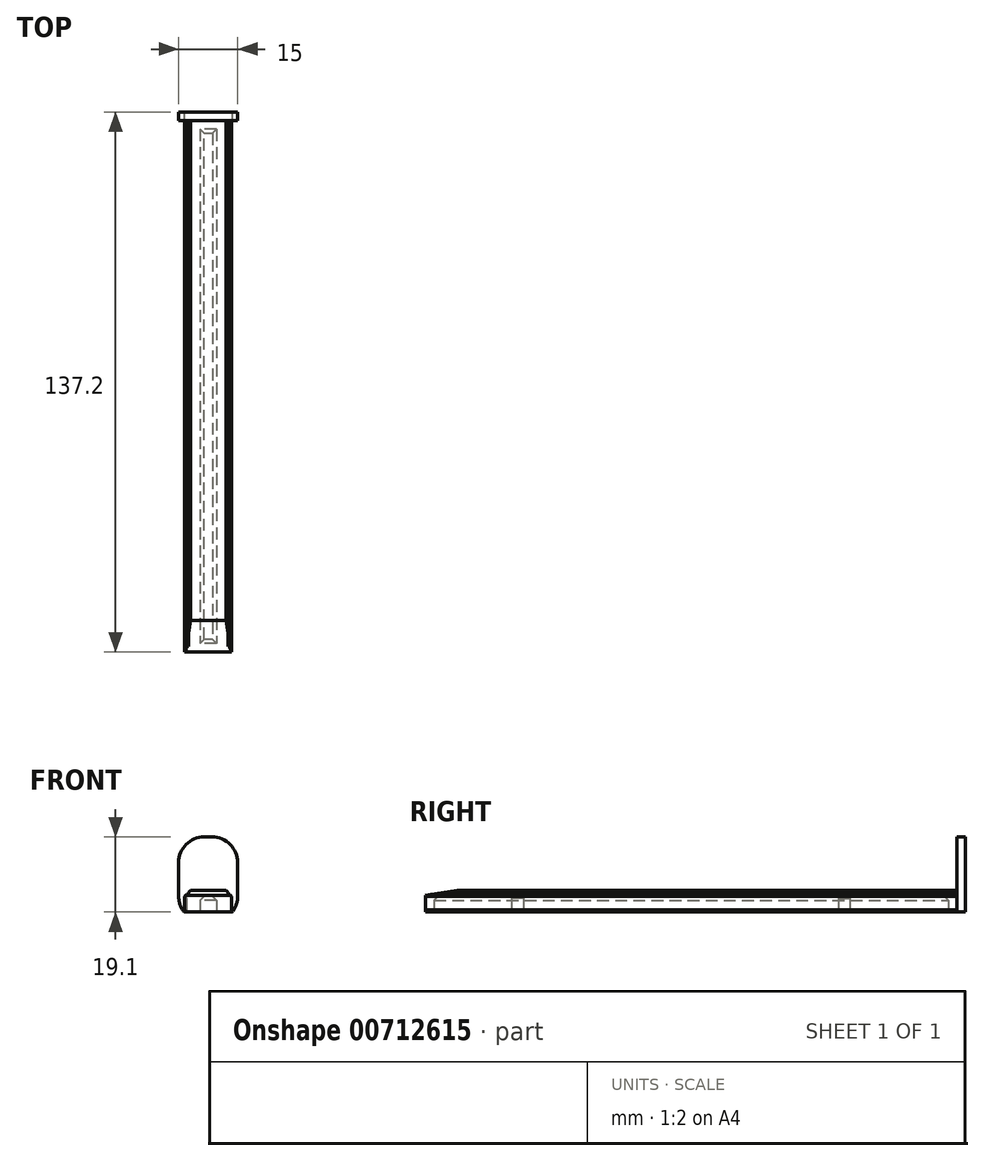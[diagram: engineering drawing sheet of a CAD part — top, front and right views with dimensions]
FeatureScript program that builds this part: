
annotation { "Feature Type Name" : "Feature", "Feature Type Description" : "" }
export const myFeature = defineFeature(function(context is Context, id is Id, definition is map)
    precondition{}
    {
        {
            var Q0;
            Q0=qCreatedBy(makeId("Front.planeOp"),FACE);
            var sketch = newSketch(context, id + "F0", { "sketchPlane" : qUnion([Q0])});
            skLineSegment(sketch, "E0.bottom", {"start": v(6, -2.75) * mm, "end": v(-6, -2.75) * mm});
            skLineSegment(sketch, "E0.top", {"start": v(5, 2.75) * mm, "end": v(-5, 2.75) * mm});
            skLineSegment(sketch, "E0.left", {"start": v(6, -2.75) * mm, "end": v(6, 1.75) * mm});
            skLineSegment(sketch, "E0.right", {"start": v(-6, -2.75) * mm, "end": v(-6, 1.75) * mm});
            skPoint(sketch, "E0.middle", {"position": v(0, 0) * mm});
            skLineSegment(sketch, "E1", {"start": v(-6, 1.75) * mm, "end": v(-5, 1.75) * mm});
            skLineSegment(sketch, "E2", {"start": v(-5, 2.75) * mm, "end": v(-5, 1.75) * mm});
            skLineSegment(sketch, "E3.MirrorCS", {"start": v(5, 2.75) * mm, "end": v(5, 1.75) * mm});
            skLineSegment(sketch, "E4.trimOffspring", {"start": v(5, 1.75) * mm, "end": v(6, 1.75) * mm});
            skPoint(sketch, "E5.orphan", {"position": v(-6, 2.75) * mm});
            skPoint(sketch, "E6.orphan", {"position": v(6, 2.75) * mm});
            skSolve(sketch);
        }
        {
            var Q0;
            Q0 = qSketchRegion(id + "F0", true);
            extrude(context, id + "F1", {"entities" : qUnion([Q0]), "depth" : 135 * mm, "offsetDistance" : 25 * mm});
        }
        {
            var Q0;
            Q0=makeQuery(id+"F1.opExtrude","CAP_EDGE",EDGE,{"disambiguationData":[OSD([sQuery(id+"F0.wireOp",EDGE,"E0.top")])],"isStart":false});
            chamfer(context, id + "F2", {"entities" : qUnion([Q0]), "chamferType" : ChamferType.TWO_OFFSETS, "width1" : 1.2 * mm, "oppositeDirection" : false, "width2" : 8 * mm, "tangentPropagation" : true});
        }
        {
            var Q0;
            Q0=qCreatedBy(makeId("Front.planeOp"),FACE);
            var sketch = newSketch(context, id + "F3", { "sketchPlane" : qUnion([Q0])});
            skLineSegment(sketch, "E7.bottom", {"start": v(1, -5.25) * mm, "end": v(-1, -5.25) * mm, "construction": true});
            skLineSegment(sketch, "E7.top", {"start": v(1, 16.35) * mm, "end": v(-1, 16.35) * mm});
            skLineSegment(sketch, "E7.left", {"start": v(7.5, 1.25) * mm, "end": v(7.5, 9.85) * mm});
            skLineSegment(sketch, "E7.right", {"start": v(-7.5, 1.25) * mm, "end": v(-7.5, 9.85) * mm});
            skLineSegment(sketch, "E8.0", {"start": v(6, -2.75) * mm, "end": v(-6, -2.75) * mm, "construction": true});
            skLineSegment(sketch, "E9.0", {"start": v(5, 2.75) * mm, "end": v(-5, 2.75) * mm, "construction": true});
            skPoint(sketch, "E10.visualSharp", {"position": v(7.5, 16.35) * mm});
            skArc(sketch, "E10.filletArc", {"start": v(7.5, 9.85) * mm, "mid": v(5.6, 14.45) * mm, "end": v(1, 16.35) * mm});
            skPoint(sketch, "E11.visualSharp", {"position": v(-7.5, 16.35) * mm});
            skArc(sketch, "E11.filletArc", {"start": v(-1, 16.35) * mm, "mid": v(-5.6, 14.45) * mm, "end": v(-7.5, 9.85) * mm});
            skPoint(sketch, "E12.visualSharp", {"position": v(-7.5, -5.25) * mm});
            skArc(sketch, "E12.filletArc", {"start": v(-7.5, 1.25) * mm, "mid": v(-7.15, -0.87) * mm, "end": v(-6.12, -2.75) * mm});
            skPoint(sketch, "E13.visualSharp", {"position": v(7.5, -5.25) * mm});
            skArc(sketch, "E13.filletArc", {"start": v(1, -5.25) * mm, "mid": v(3.85, -4.6) * mm, "end": v(6.12, -2.75) * mm, "construction": true});
            skLineSegment(sketch, "E14", {"start": v(-6.12, -2.75) * mm, "end": v(6.12, -2.75) * mm});
            skArc(sketch, "E15", {"start": v(6.12, -2.75) * mm, "mid": v(7.15, -0.87) * mm, "end": v(7.5, 1.25) * mm});
            skArc(sketch, "E16", {"start": v(-6.12, -2.75) * mm, "mid": v(-3.85, -4.6) * mm, "end": v(-1, -5.25) * mm, "construction": true});
            skSolve(sketch);
        }
        {
            var Q0;
            Q0 = qSketchRegion(id + "F3", true);
            extrude(context, id + "F4", {"entities" : qUnion([Q0]), "operationType" : NewBodyOperationType.ADD, "oppositeDirection" : true, "depth" : 2.2 * mm, "offsetDistance" : 25 * mm});
        }
        {
            var Q0;
            Q0=makeQuery(id+"F1.opExtrude","SWEPT_FACE",FACE,{"disambiguationData":[OSD([sQuery(id+"F0.wireOp",EDGE,"E0.right")])]});
            var sketch = newSketch(context, id + "F5", { "sketchPlane" : qUnion([Q0])});
            skLineSegment(sketch, "E17.0", {"start": v(0, -2.75) * mm, "end": v(0, -2.75) * mm});
            skLineSegment(sketch, "E18.0", {"start": v(135, -2.75) * mm, "end": v(0, -2.75) * mm, "construction": true});
            skLineSegment(sketch, "E19.bottom", {"start": v(30, -2.25) * mm, "end": v(27, -2.25) * mm});
            skLineSegment(sketch, "E19.top", {"start": v(30, 0.75) * mm, "end": v(27, 0.75) * mm});
            skLineSegment(sketch, "E19.left", {"start": v(30, -2.25) * mm, "end": v(30, 0.75) * mm});
            skLineSegment(sketch, "E19.right", {"start": v(27, -2.25) * mm, "end": v(27, 0.75) * mm});
            skLineSegment(sketch, "E20.bottom", {"start": v(110, -2.25) * mm, "end": v(110, 0.75) * mm});
            skLineSegment(sketch, "E20.top", {"start": v(113, -2.25) * mm, "end": v(113, 0.75) * mm});
            skLineSegment(sketch, "E20.left", {"start": v(110, -2.25) * mm, "end": v(113, -2.25) * mm});
            skLineSegment(sketch, "E20.right", {"start": v(110, 0.75) * mm, "end": v(113, 0.75) * mm});
            skSolve(sketch);
        }
        {
            var Q0;
            Q0 = qSketchRegion(id + "F5", true);
            extrude(context, id + "F6", {"entities" : qUnion([Q0]), "operationType" : NewBodyOperationType.REMOVE, "oppositeDirection" : true, "depth" : 0.7 * mm, "offsetDistance" : 25 * mm});
        }
        {
            var Q0;
            Q0=makeQuery(id+"F1.opExtrude","SWEPT_EDGE",EDGE,{"disambiguationData":[OSD([sQuery(id+"F0.wireOp",EDGE,"E0.top"),sQuery(id+"F0.wireOp",EDGE,"E0.right")])]});
            var Q1;
            Q1=makeQuery(id+"F1.opExtrude","SWEPT_EDGE",EDGE,{"disambiguationData":[OSD([sQuery(id+"F0.wireOp",EDGE,"E0.top"),sQuery(id+"F0.wireOp",EDGE,"E0.left")])]});
            chamfer(context, id + "F7", {"entities" : qUnion([Q0, Q1]), "width" : 0.5 * mm});
        }
        {
            var Q0;
            Q0=makeQuery(id+"F4.boolean.opBoolean","MERGE",FACE,{"derivedFrom":[makeQuery(id+"F1.opExtrude","SWEPT_FACE",FACE,{"disambiguationData":[OSD([sQuery(id+"F0.wireOp",EDGE,"E0.bottom")])]}),makeQuery(id+"F4.opExtrude","SWEPT_FACE",FACE,{"disambiguationData":[OSD([sQuery(id+"F3.wireOp",EDGE,"E14")])]})]});
            var sketch = newSketch(context, id + "F8", { "sketchPlane" : qUnion([Q0])});
            skLineSegment(sketch, "E21", {"start": v(2.1, 0) * mm, "end": v(2.1, 135) * mm});
            skLineSegment(sketch, "E22.MirrorCS", {"start": v(-2.1, 0) * mm, "end": v(-2.1, 135) * mm});
            skLineSegment(sketch, "E23", {"start": v(2.1, 132.8) * mm, "end": v(-2.1, 132.8) * mm});
            skLineSegment(sketch, "E24", {"start": v(2.1, 2.2) * mm, "end": v(-2.1, 2.2) * mm});
            skSolve(sketch);
        }
        {
            var Q0;
            Q0 = qSketchRegion(id + "F8", true);
            extrude(context, id + "F9", {"entities" : qUnion([Q0]), "operationType" : NewBodyOperationType.REMOVE, "oppositeDirection" : true, "depth" : 4 * mm, "offsetDistance" : 25 * mm});
        }
        {
            var Q0;
            Q0=makeQuery(id+"F9.boolean.opBoolean","COPY",EDGE,{"derivedFrom":makeQuery(id+"F9.opExtrude","CAP_EDGE",EDGE,{"disambiguationData":[OSD([sQuery(id+"F8.wireOp",EDGE,"E23")])],"isStart":false})});
            var Q1;
            Q1=makeQuery(id+"F9.boolean.opBoolean","COPY",EDGE,{"derivedFrom":makeQuery(id+"F9.opExtrude","CAP_EDGE",EDGE,{"disambiguationData":[OSD([sQuery(id+"F8.wireOp",EDGE,"E22.MirrorCS")])],"isStart":false})});
            var Q2;
            Q2=makeQuery(id+"F9.boolean.opBoolean","COPY",EDGE,{"derivedFrom":makeQuery(id+"F9.opExtrude","CAP_EDGE",EDGE,{"disambiguationData":[OSD([sQuery(id+"F8.wireOp",EDGE,"E21")])],"isStart":false})});
            var Q3;
            Q3=makeQuery(id+"F9.boolean.opBoolean","COPY",EDGE,{"derivedFrom":makeQuery(id+"F9.opExtrude","CAP_EDGE",EDGE,{"disambiguationData":[OSD([sQuery(id+"F8.wireOp",EDGE,"E24")])],"isStart":false})});
            var Q4;
            Q4=makeQuery(id+"F9.boolean.opBoolean","COPY",EDGE,{"derivedFrom":makeQuery(id+"F9.opExtrude","CAP_EDGE",EDGE,{"disambiguationData":[OSD([sQuery(id+"F8.wireOp",EDGE,"E21")])],"isStart":true})});
            var Q5;
            Q5=makeQuery(id+"F9.boolean.opBoolean","COPY",EDGE,{"derivedFrom":makeQuery(id+"F9.opExtrude","CAP_EDGE",EDGE,{"disambiguationData":[OSD([sQuery(id+"F8.wireOp",EDGE,"E22.MirrorCS")])],"isStart":true})});
            chamfer(context, id + "F10", {"entities" : qUnion([Q0, Q1, Q2, Q3, Q4, Q5]), "width" : 1 * mm, "tangentPropagation" : true});
        }
    });
